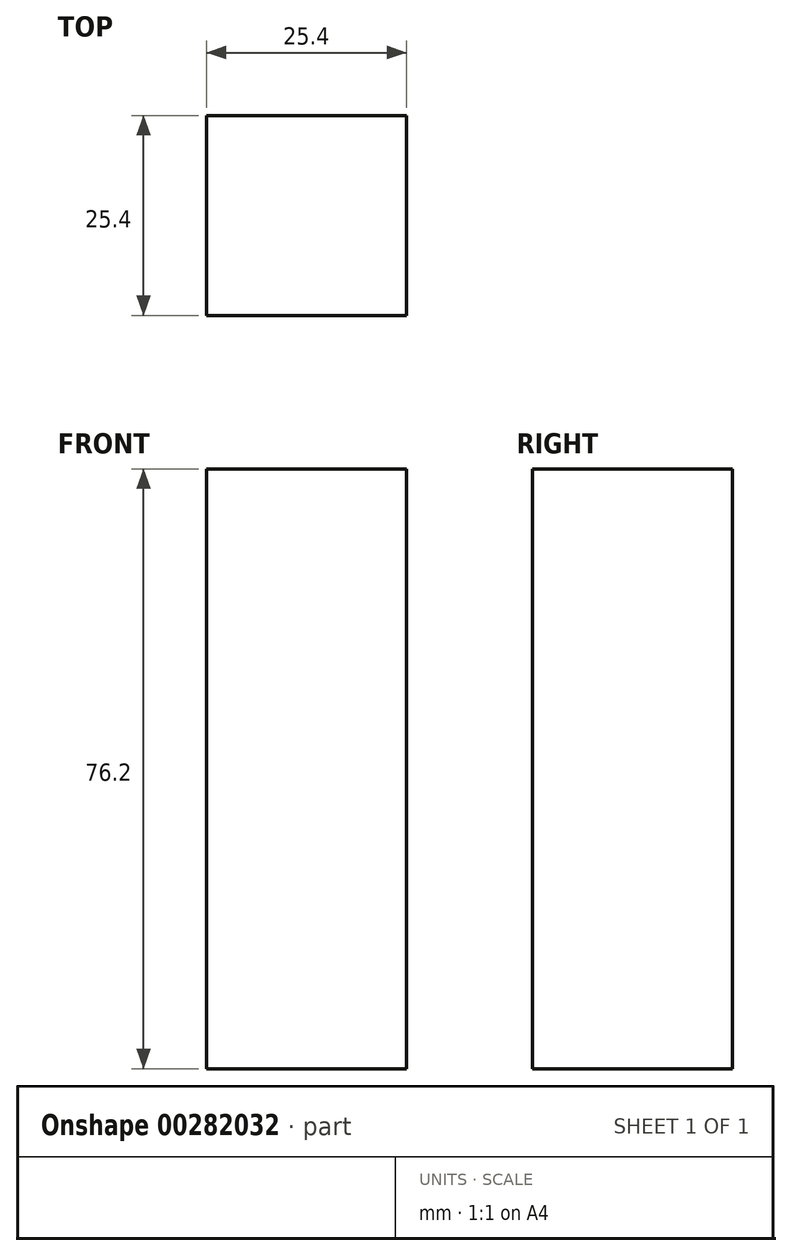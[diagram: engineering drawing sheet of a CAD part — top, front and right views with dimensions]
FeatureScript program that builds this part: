
annotation { "Feature Type Name" : "Feature", "Feature Type Description" : "" }
export const myFeature = defineFeature(function(context is Context, id is Id, definition is map)
    precondition{}
    {
        {
            var Q0;
            Q0=qCreatedBy(makeId("Front.planeOp"),FACE);
            var sketch = newSketch(context, id + "F0", { "sketchPlane" : qUnion([Q0])});
            skLineSegment(sketch, "E0.bottom", {"start": v(-29.41, 69.7) * mm, "end": v(-4.01, 69.7) * mm});
            skLineSegment(sketch, "E0.top", {"start": v(-29.41, -6.5) * mm, "end": v(-4.01, -6.5) * mm});
            skLineSegment(sketch, "E0.left", {"start": v(-29.41, 69.7) * mm, "end": v(-29.41, -6.5) * mm});
            skLineSegment(sketch, "E0.right", {"start": v(-4.01, 69.7) * mm, "end": v(-4.01, -6.5) * mm});
            skSolve(sketch);
        }
        {
            var Q0;
            Q0 = qSketchRegion(id + "F0", true);
            extrude(context, id + "F1", {"entities" : qUnion([Q0]), "depth" : 25.4 * mm});
        }
    });
